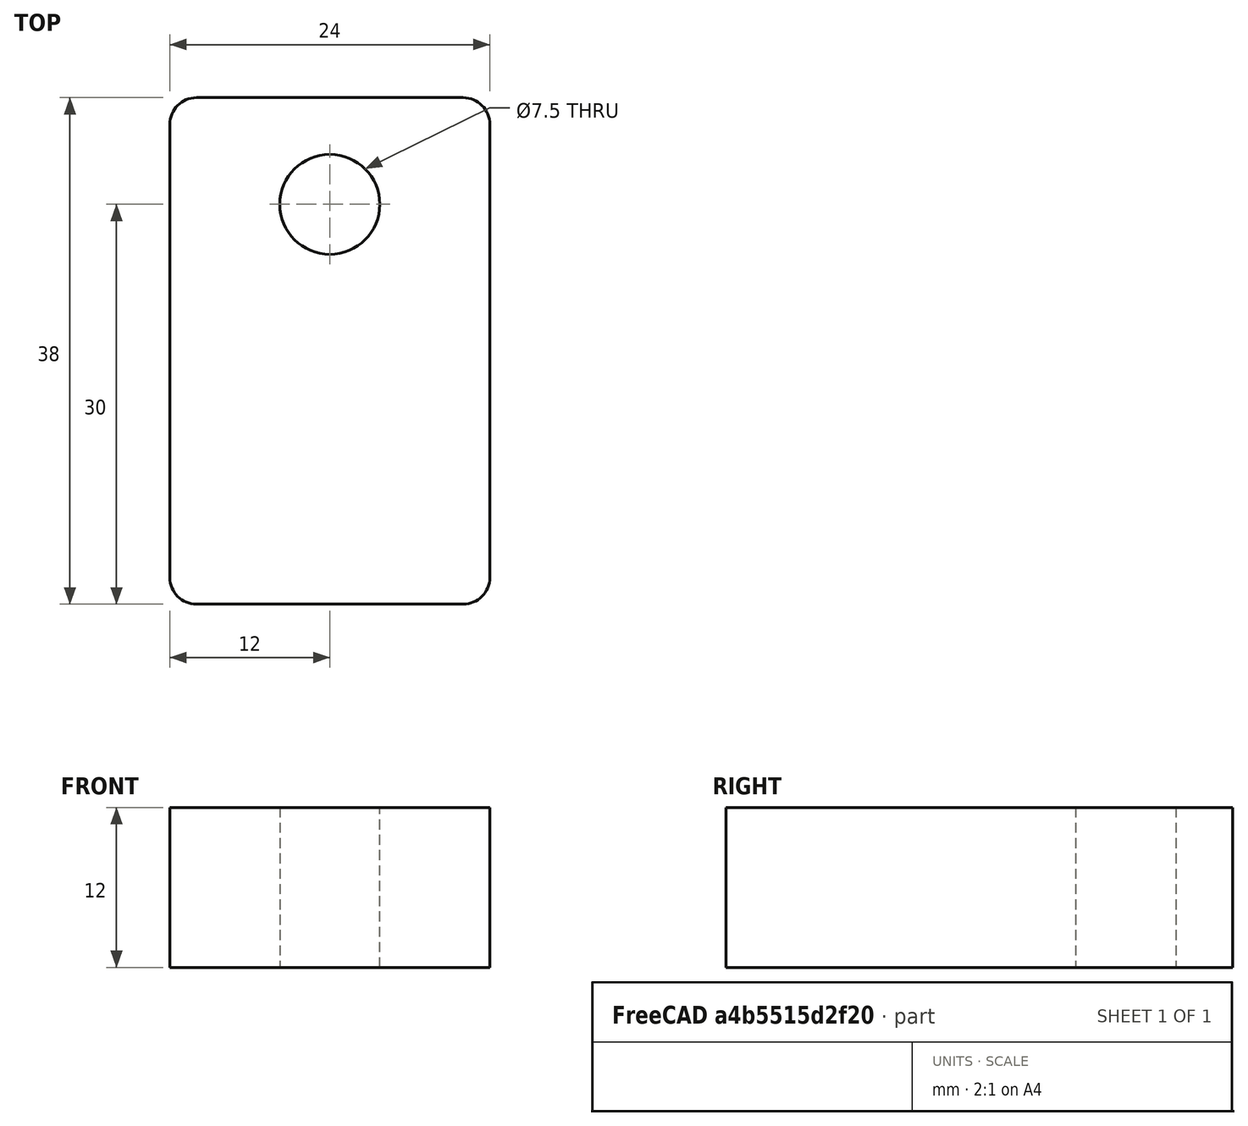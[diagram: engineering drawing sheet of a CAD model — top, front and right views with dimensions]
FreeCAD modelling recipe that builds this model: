
FCSTD DOCUMENT  (FreeCAD 0.19R24366 (Git))
Label: Camera spacer plate 12mm
License: All rights reserved
LicenseURL: http://en.wikipedia.org/wiki/All_rights_reserved
objects: Sketcher::SketchObject×1, PartDesign::Pad×1, PartDesign::Body×1
note: 4 computed .brp shape members not serialized (recipe doc carries the construction recipe); baked Part::Feature solids carry a one-line shape summary decoded from their .brp

FEATURE [Sketcher::SketchObject] Sketch
  FullyConstrained = true
  MapMode = 5
  Support = -> [XY_Plane]
  sketch-geometry (9):
    g0: Circle CenterX=0 CenterY=0 CenterZ=0 NormalX=0 NormalY=0 NormalZ=1 AngleXU=0 Radius=3.75
    g1: LineSegment StartX=-10 StartY=8 StartZ=0 EndX=10 EndY=8 EndZ=0
    g2: LineSegment StartX=-10 StartY=-30 StartZ=0 EndX=10 EndY=-30 EndZ=0
    g3: LineSegment StartX=-12 StartY=6 StartZ=0 EndX=-12 EndY=-28 EndZ=0
    g4: LineSegment StartX=12 StartY=-28 StartZ=0 EndX=12 EndY=6 EndZ=0
    g5: ArcOfCircle CenterX=-10 CenterY=6 CenterZ=0 NormalX=0 NormalY=0 NormalZ=1 AngleXU=0 Radius=2 StartAngle=1.5708 EndAngle=3.14159
    g6: ArcOfCircle CenterX=10 CenterY=6 CenterZ=0 NormalX=0 NormalY=0 NormalZ=1 AngleXU=0 Radius=2 StartAngle=0 EndAngle=1.5708
    g7: ArcOfCircle CenterX=10 CenterY=-28 CenterZ=0 NormalX=0 NormalY=0 NormalZ=1 AngleXU=0 Radius=2 StartAngle=4.71239 EndAngle=6.28319
    g8: ArcOfCircle CenterX=-10 CenterY=-28 CenterZ=0 NormalX=0 NormalY=0 NormalZ=1 AngleXU=0 Radius=2 StartAngle=3.14159 EndAngle=4.71239
  constraints (21):
    c: Coincident(g0,g-1)
    c: Horizontal(g2)
    c: Vertical(g3)
    c: Vertical(g4)
    c: Tangent(g1,g5) = 1.5708
    c: Tangent(g3,g5) = -1.5708
    c: Tangent(g1,g6) = 1.5708
    c: Tangent(g4,g6) = -1.5708
    c: Tangent(g4,g7) = -1.5708
    c: Tangent(g2,g7) = -1.5708
    c: Tangent(g3,g8) = -1.5708
    c: Tangent(g2,g8) = -1.5708
    c: Equal(g5,g6)
    c: Equal(g6,g7)
    c: Equal(g7,g8)
    c: Radius(g5) = 2
    c: Symmetric(g1,g1,g-2)
    c: DistanceY(g0,g1) = 8
    c: DistanceY(g2,g0) = 30
    c: Diameter(g0) = 7.5
    c: DistanceX(g1,g1) = 20
FEATURE [PartDesign::Pad] Pad
  Direction = (1,1,1)
  Length = 12
  Length2 = 100
  Profile = -> Sketch
  Type = 0
FEATURE [PartDesign::Body] Body
  Group = -> [Sketch,Pad]
  Origin = -> Origin
  Tip = -> Pad
